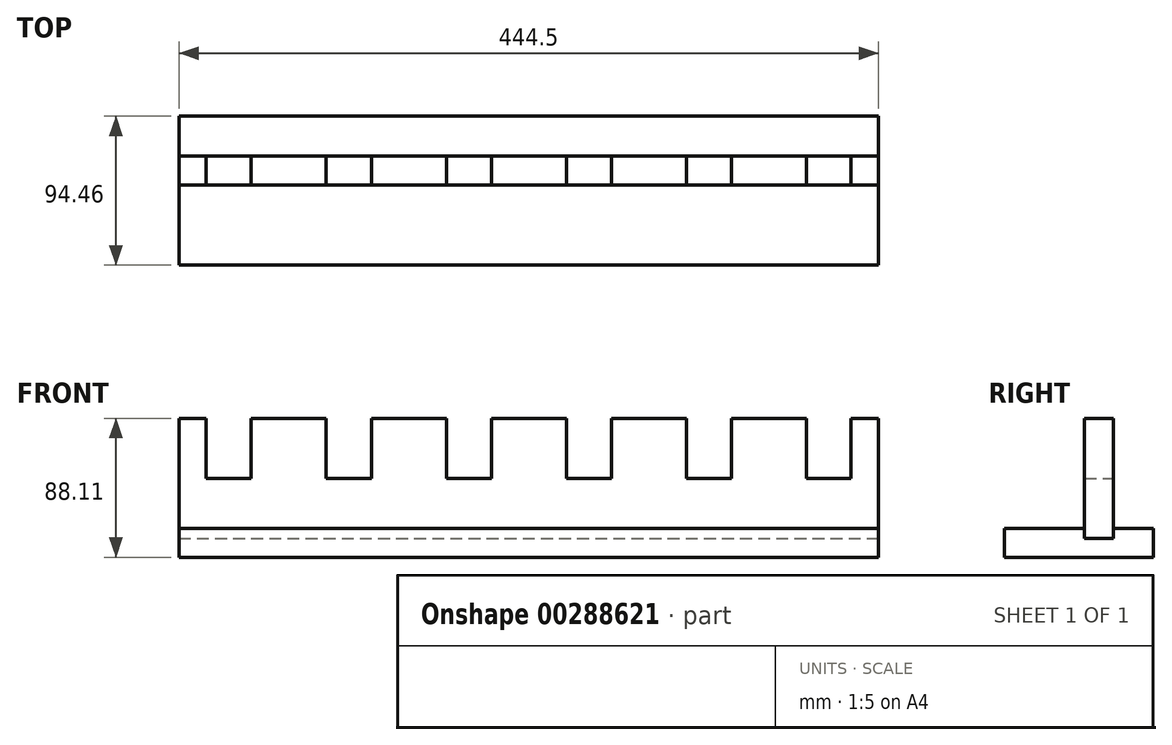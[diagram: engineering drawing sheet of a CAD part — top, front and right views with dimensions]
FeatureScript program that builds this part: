
annotation { "Feature Type Name" : "Feature", "Feature Type Description" : "" }
export const myFeature = defineFeature(function(context is Context, id is Id, definition is map)
    precondition{}
    {
        {
            var Q0;
            Q0=qCreatedBy(makeId("Front.planeOp"),FACE);
            var sketch = newSketch(context, id + "F0", { "sketchPlane" : qUnion([Q0])});
            skLineSegment(sketch, "E0.bottom", {"start": v(-222.25, 38.1) * mm, "end": v(-204.79, 38.1) * mm});
            skLineSegment(sketch, "E0.top", {"start": v(-222.25, -38.1) * mm, "end": v(222.25, -38.1) * mm});
            skLineSegment(sketch, "E0.left", {"start": v(-222.25, 38.1) * mm, "end": v(-222.25, -38.1) * mm});
            skLineSegment(sketch, "E0.right", {"start": v(222.25, 38.1) * mm, "end": v(222.25, -38.1) * mm});
            skLineSegment(sketch, "E1.top", {"start": v(-204.79, 0) * mm, "end": v(-176.21, 0) * mm});
            skLineSegment(sketch, "E1.left", {"start": v(-204.79, 38.1) * mm, "end": v(-204.79, 0) * mm});
            skLineSegment(sketch, "E1.right", {"start": v(-176.21, 38.1) * mm, "end": v(-176.21, 0) * mm});
            skLineSegment(sketch, "E2.1.0.0", {"start": v(-100.01, 38.1) * mm, "end": v(-100.01, 0) * mm});
            skLineSegment(sketch, "E2.1.0.1", {"start": v(-128.59, 38.1) * mm, "end": v(-128.59, 0) * mm});
            skLineSegment(sketch, "E2.1.0.2", {"start": v(-128.59, 0) * mm, "end": v(-100.01, 0) * mm});
            skLineSegment(sketch, "E2.2.0.0", {"start": v(-23.81, 38.1) * mm, "end": v(-23.81, 0) * mm});
            skLineSegment(sketch, "E2.2.0.1", {"start": v(-52.39, 38.1) * mm, "end": v(-52.39, 0) * mm});
            skLineSegment(sketch, "E2.2.0.2", {"start": v(-52.39, 0) * mm, "end": v(-23.81, 0) * mm});
            skLineSegment(sketch, "E2.3.0.0", {"start": v(52.39, 38.1) * mm, "end": v(52.39, 0) * mm});
            skLineSegment(sketch, "E2.3.0.1", {"start": v(23.81, 38.1) * mm, "end": v(23.81, 0) * mm});
            skLineSegment(sketch, "E2.3.0.2", {"start": v(23.81, 0) * mm, "end": v(52.39, 0) * mm});
            skLineSegment(sketch, "E2.direction1", {"start": v(-204.79, 0) * mm, "end": v(-128.59, 0) * mm, "construction": true});
            skLineSegment(sketch, "E3", {"start": v(-204.79, 0) * mm, "end": v(-222.25, 0) * mm, "construction": true});
            skLineSegment(sketch, "E4", {"start": v(-222.25, -31.75) * mm, "end": v(222.25, -31.75) * mm, "construction": true});
            skLineSegment(sketch, "E5.trimOffspring", {"start": v(-176.21, 38.1) * mm, "end": v(-128.59, 38.1) * mm});
            skLineSegment(sketch, "E6", {"start": v(-100.01, 38.1) * mm, "end": v(-52.39, 38.1) * mm});
            skLineSegment(sketch, "E7", {"start": v(-23.81, 38.1) * mm, "end": v(23.81, 38.1) * mm});
            skLineSegment(sketch, "E8.0.4.0", {"start": v(128.59, 38.1) * mm, "end": v(128.59, 0) * mm});
            skLineSegment(sketch, "E8.3.4.0", {"start": v(100.01, 38.1) * mm, "end": v(100.01, 0) * mm});
            skLineSegment(sketch, "E8.6.4.0", {"start": v(100.01, 0) * mm, "end": v(128.59, 0) * mm});
            skLineSegment(sketch, "E9.0.5.0", {"start": v(204.79, 38.1) * mm, "end": v(204.79, 0) * mm});
            skLineSegment(sketch, "E9.3.5.0", {"start": v(176.21, 38.1) * mm, "end": v(176.21, 0) * mm});
            skLineSegment(sketch, "E9.6.5.0", {"start": v(176.21, 0) * mm, "end": v(204.79, 0) * mm});
            skLineSegment(sketch, "E10", {"start": v(204.79, 38.1) * mm, "end": v(222.25, 38.1) * mm});
            skLineSegment(sketch, "E11", {"start": v(52.39, 38.1) * mm, "end": v(100.01, 38.1) * mm});
            skLineSegment(sketch, "E12", {"start": v(128.59, 38.1) * mm, "end": v(176.21, 38.1) * mm});
            skSolve(sketch);
        }
        {
            var Q0;
            Q0=makeQuery(id+"F0.imprint","IMPRINT",FACE,{"disambiguationData":[TD([[makeQuery(id+"F0.imprint","IMPRINT",EDGE,{"derivedFrom":sQuery(id+"F0.wireOp",EDGE,"E0.bottom")}),-1.0]])]});
            extrude(context, id + "F1", {"entities" : qUnion([Q0]), "depth" : 18.26 * mm});
        }
        {
            var Q0;
            Q0=makeQuery(id+"F1.opExtrude","SWEPT_FACE",FACE,{"disambiguationData":[OSD([sQuery(id+"F0.wireOp",EDGE,"E0.right")])]});
            var sketch = newSketch(context, id + "F2", { "sketchPlane" : qUnion([Q0])});
            skLineSegment(sketch, "E13", {"start": v(0, -31.75) * mm, "end": v(0, -38.1) * mm});
            skLineSegment(sketch, "E14", {"start": v(0, -38.1) * mm, "end": v(-18.26, -38.1) * mm});
            skLineSegment(sketch, "E15", {"start": v(-18.26, -38.1) * mm, "end": v(-18.26, -31.75) * mm});
            skLineSegment(sketch, "E16", {"start": v(0, -31.75) * mm, "end": v(25.4, -31.75) * mm});
            skLineSegment(sketch, "E17", {"start": v(25.4, -31.75) * mm, "end": v(25.4, -50) * mm});
            skLineSegment(sketch, "E18", {"start": v(25.4, -50) * mm, "end": v(-69.06, -50) * mm});
            skLineSegment(sketch, "E19", {"start": v(-69.06, -50) * mm, "end": v(-69.06, -31.75) * mm});
            skLineSegment(sketch, "E20", {"start": v(-18.26, -31.75) * mm, "end": v(-69.06, -31.75) * mm});
            skSolve(sketch);
        }
        {
            var Q0;
            Q0=makeQuery(id+"F2.imprint","IMPRINT",FACE,{"disambiguationData":[TD([[makeQuery(id+"F2.imprint","IMPRINT",EDGE,{"derivedFrom":sQuery(id+"F2.wireOp",EDGE,"E13")}),1.0]])]});
            var Q1;
            Q1=makeQuery(id+"F1.opExtrude","SWEPT_FACE",FACE,{"disambiguationData":[OSD([sQuery(id+"F0.wireOp",EDGE,"E0.left")])]});
            extrude(context, id + "F3", {"entities" : qUnion([Q0]), "endBound" : BoundingType.UP_TO_SURFACE, "oppositeDirection" : true, "endBoundEntityFace" : qUnion([Q1]), "depth" : 25.4 * mm});
        }
    });
